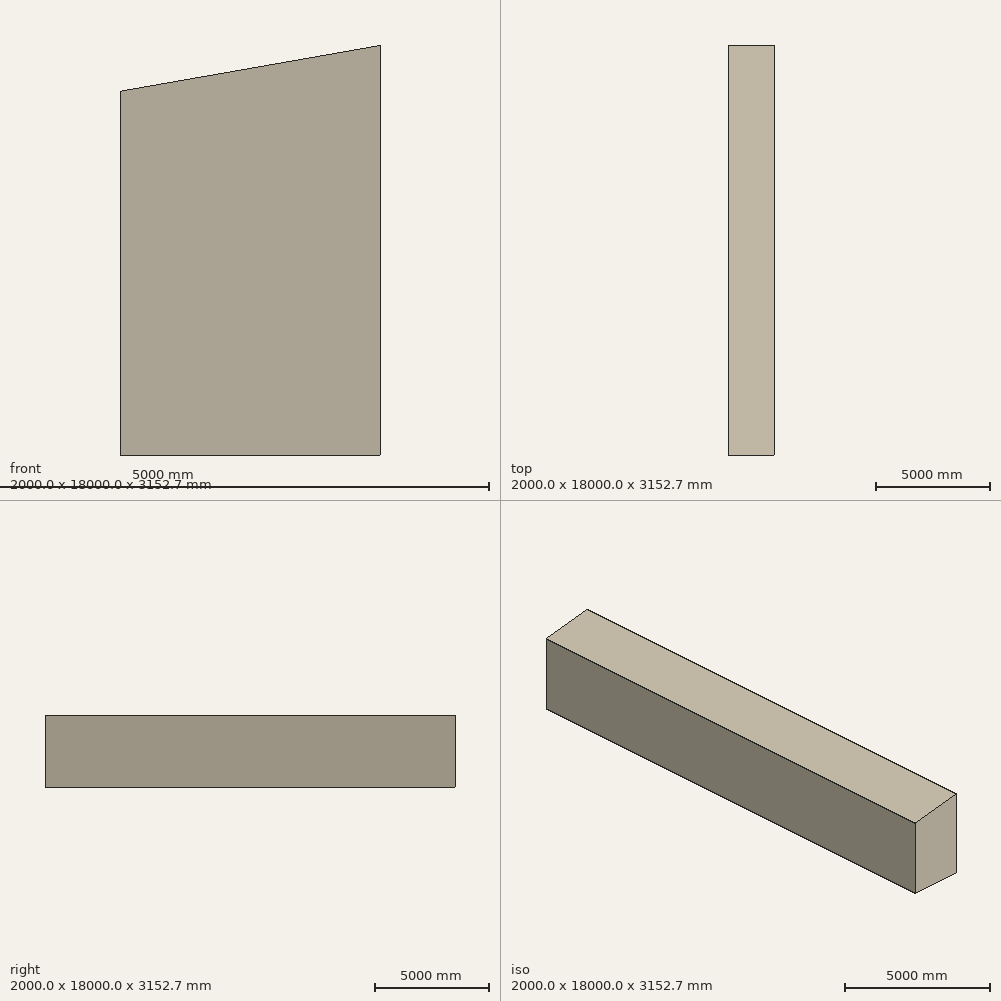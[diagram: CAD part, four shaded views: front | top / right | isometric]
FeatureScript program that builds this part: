
annotation { "Feature Type Name" : "Feature", "Feature Type Description" : "" }
export const myFeature = defineFeature(function(context is Context, id is Id, definition is map)
    precondition{}
    {
        {
            var Q0;
            Q0=qCreatedBy(makeId("Front.planeOp"),FACE);
            var sketch = newSketch(context, id + "F0", { "sketchPlane" : qUnion([Q0])});
            skLineSegment(sketch, "E0", {"start": v(0, 0) * mm, "end": v(-2000, 0) * mm});
            skLineSegment(sketch, "E1", {"start": v(-2000, 0) * mm, "end": v(-2000, 2800) * mm});
            skLineSegment(sketch, "E2", {"start": v(-2000, 2800) * mm, "end": v(0, 3152.65) * mm});
            skLineSegment(sketch, "E3", {"start": v(0, 3152.65) * mm, "end": v(0, 0) * mm});
            skSolve(sketch);
        }
        {
            var Q0;
            Q0 = qSketchRegion(id + "F0", true);
            extrude(context, id + "F1", {"entities" : qUnion([Q0]), "depth" : 18000 * mm});
        }
    });
